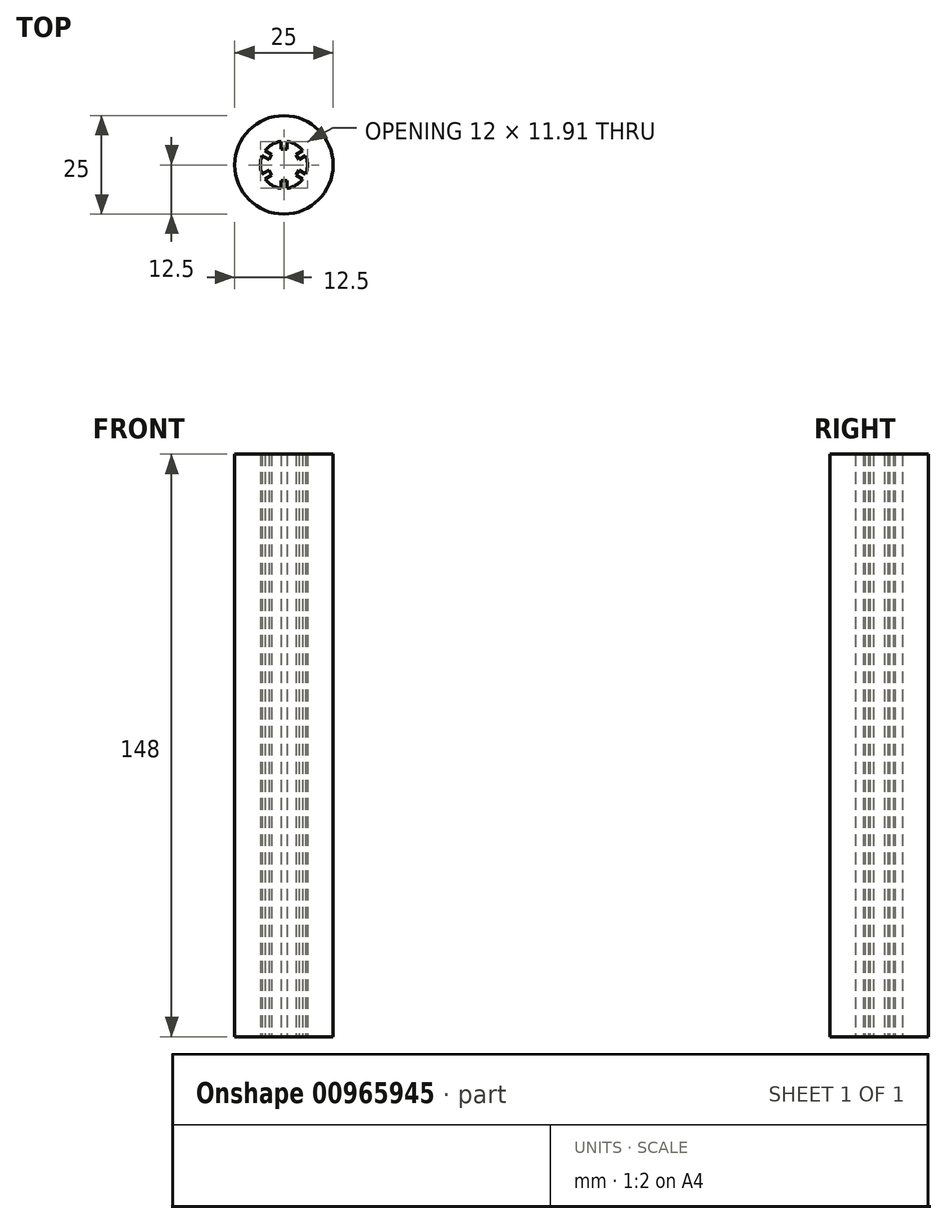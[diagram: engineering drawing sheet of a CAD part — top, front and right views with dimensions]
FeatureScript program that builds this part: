
annotation { "Feature Type Name" : "Feature", "Feature Type Description" : "" }
export const myFeature = defineFeature(function(context is Context, id is Id, definition is map)
    precondition{}
    {
        {
            var Q0;
            Q0=qCreatedBy(makeId("Top.planeOp"),FACE);
            var sketch = newSketch(context, id + "F0", { "sketchPlane" : qUnion([Q0])});
            skCircle(sketch, "E0", {"center": v(0, 0) * mm, "radius": 4 * mm, "construction": true});
            skCircle(sketch, "E1", {"center": v(0, 0) * mm, "radius": 6 * mm});
            skCircle(sketch, "E2", {"center": v(0, 0) * mm, "radius": 12.5 * mm});
            skLineSegment(sketch, "E3.bottom", {"start": v(-0.75, 6) * mm, "end": v(0.75, 6) * mm});
            skLineSegment(sketch, "E3.top", {"start": v(-0.75, 4) * mm, "end": v(0.75, 4) * mm});
            skLineSegment(sketch, "E3.left", {"start": v(-0.75, 6) * mm, "end": v(-0.75, 4) * mm});
            skLineSegment(sketch, "E3.right", {"start": v(0.75, 6) * mm, "end": v(0.75, 4) * mm});
            skLineSegment(sketch, "E4.1.0", {"start": v(-5.57, 2.35) * mm, "end": v(-3.84, 1.35) * mm});
            skLineSegment(sketch, "E4.1.1", {"start": v(-4.82, 3.65) * mm, "end": v(-3.09, 2.65) * mm});
            skLineSegment(sketch, "E4.1.2", {"start": v(-3.84, 1.35) * mm, "end": v(-3.09, 2.65) * mm});
            skLineSegment(sketch, "E4.1.3", {"start": v(-5.57, 2.35) * mm, "end": v(-4.82, 3.65) * mm});
            skLineSegment(sketch, "E4.2.0", {"start": v(-4.82, -3.65) * mm, "end": v(-3.09, -2.65) * mm});
            skLineSegment(sketch, "E4.2.1", {"start": v(-5.57, -2.35) * mm, "end": v(-3.84, -1.35) * mm});
            skLineSegment(sketch, "E4.2.2", {"start": v(-3.09, -2.65) * mm, "end": v(-3.84, -1.35) * mm});
            skLineSegment(sketch, "E4.2.3", {"start": v(-4.82, -3.65) * mm, "end": v(-5.57, -2.35) * mm});
            skLineSegment(sketch, "E5.2.3.0", {"start": v(0.75, -6) * mm, "end": v(0.75, -4) * mm});
            skLineSegment(sketch, "E5.3.3.0", {"start": v(-0.75, -6) * mm, "end": v(-0.75, -4) * mm});
            skLineSegment(sketch, "E5.6.3.0", {"start": v(0.75, -4) * mm, "end": v(-0.75, -4) * mm});
            skLineSegment(sketch, "E5.9.3.0", {"start": v(0.75, -6) * mm, "end": v(-0.75, -6) * mm});
            skLineSegment(sketch, "E5.2.4.0", {"start": v(5.57, -2.35) * mm, "end": v(3.84, -1.35) * mm});
            skLineSegment(sketch, "E5.3.4.0", {"start": v(4.82, -3.65) * mm, "end": v(3.09, -2.65) * mm});
            skLineSegment(sketch, "E5.6.4.0", {"start": v(3.84, -1.35) * mm, "end": v(3.09, -2.65) * mm});
            skLineSegment(sketch, "E5.9.4.0", {"start": v(5.57, -2.35) * mm, "end": v(4.82, -3.65) * mm});
            skLineSegment(sketch, "E5.2.5.0", {"start": v(4.82, 3.65) * mm, "end": v(3.09, 2.65) * mm});
            skLineSegment(sketch, "E5.3.5.0", {"start": v(5.57, 2.35) * mm, "end": v(3.84, 1.35) * mm});
            skLineSegment(sketch, "E5.6.5.0", {"start": v(3.09, 2.65) * mm, "end": v(3.84, 1.35) * mm});
            skLineSegment(sketch, "E5.9.5.0", {"start": v(4.82, 3.65) * mm, "end": v(5.57, 2.35) * mm});
            skPoint(sketch, "E6", {"position": v(0, 4) * mm});
            skSolve(sketch);
        }
        {
            var Q0;
            Q0=makeQuery(id+"F0.imprint","IMPRINT",FACE,{"disambiguationData":[TD([[makeQuery(id+"F0.imprint","IMPRINT",EDGE,{"derivedFrom":sQuery(id+"F0.wireOp",EDGE,"E2")}),1.0]])]});
            var Q1;
            {var subQ0=sQuery(id+"F0.wireOp",EDGE,"E4.1.2");Q1=makeQuery(id+"F0.imprint","IMPRINT",FACE,{"disambiguationData":[TD([[makeQuery(id+"F0.imprint","IMPRINT",EDGE,{"derivedFrom":subQ0}),1.0]])]});}
            var Q2;
            {var subQ0=sQuery(id+"F0.wireOp",EDGE,"E3.top");Q2=makeQuery(id+"F0.imprint","IMPRINT",FACE,{"disambiguationData":[TD([[makeQuery(id+"F0.imprint","IMPRINT",EDGE,{"derivedFrom":subQ0}),1.0]])]});}
            var Q3;
            {var subQ0=sQuery(id+"F0.wireOp",EDGE,"E5.6.5.0");Q3=makeQuery(id+"F0.imprint","IMPRINT",FACE,{"disambiguationData":[TD([[makeQuery(id+"F0.imprint","IMPRINT",EDGE,{"derivedFrom":subQ0}),1.0]])]});}
            var Q4;
            {var subQ0=sQuery(id+"F0.wireOp",EDGE,"E5.6.4.0");Q4=makeQuery(id+"F0.imprint","IMPRINT",FACE,{"disambiguationData":[TD([[makeQuery(id+"F0.imprint","IMPRINT",EDGE,{"derivedFrom":subQ0}),1.0]])]});}
            var Q5;
            {var subQ0=sQuery(id+"F0.wireOp",EDGE,"E5.6.3.0");Q5=makeQuery(id+"F0.imprint","IMPRINT",FACE,{"disambiguationData":[TD([[makeQuery(id+"F0.imprint","IMPRINT",EDGE,{"derivedFrom":subQ0}),1.0]])]});}
            var Q6;
            {var subQ0=sQuery(id+"F0.wireOp",EDGE,"E4.2.2");Q6=makeQuery(id+"F0.imprint","IMPRINT",FACE,{"disambiguationData":[TD([[makeQuery(id+"F0.imprint","IMPRINT",EDGE,{"derivedFrom":subQ0}),1.0]])]});}
            var Q7;
            {var subQ0=sQuery(id+"F0.wireOp",EDGE,"E3.right");var subQ1=sQuery(id+"F0.wireOp",EDGE,"E1");var subQ2=makeQuery(id+"F0.imprint","INTERSECT",VERTEX,{"derivedFrom":[subQ1,subQ0]});Q7=makeQuery(id+"F0.imprint","IMPRINT",FACE,{"disambiguationData":[TD([[makeQuery(id+"F0.imprint","IMPRINT",EDGE,{"disambiguationData":[TD([[subQ2,-1.0]])],"derivedFrom":subQ1}),-1.0]])]});}
            var Q8;
            {var subQ0=sQuery(id+"F0.wireOp",EDGE,"E3.bottom");var subQ1=sQuery(id+"F0.wireOp",EDGE,"E1");var subQ2=makeQuery(id+"F0.imprint","INTERSECT",VERTEX,{"derivedFrom":[subQ1,subQ0]});Q8=makeQuery(id+"F0.imprint","IMPRINT",FACE,{"disambiguationData":[TD([[makeQuery(id+"F0.imprint","IMPRINT",EDGE,{"disambiguationData":[TD([[subQ2,-1.0]])],"derivedFrom":subQ1}),-1.0]])]});}
            var Q9;
            {var subQ0=sQuery(id+"F0.wireOp",EDGE,"E4.1.1");var subQ1=sQuery(id+"F0.wireOp",EDGE,"E1");var subQ2=makeQuery(id+"F0.imprint","INTERSECT",VERTEX,{"derivedFrom":[subQ1,subQ0]});Q9=makeQuery(id+"F0.imprint","IMPRINT",FACE,{"disambiguationData":[TD([[makeQuery(id+"F0.imprint","IMPRINT",EDGE,{"disambiguationData":[TD([[subQ2,-1.0]])],"derivedFrom":subQ1}),-1.0]])]});}
            var Q10;
            {var subQ0=sQuery(id+"F0.wireOp",EDGE,"E5.9.5.0");var subQ1=sQuery(id+"F0.wireOp",EDGE,"E1");var subQ2=makeQuery(id+"F0.imprint","INTERSECT",VERTEX,{"derivedFrom":[subQ1,subQ0]});Q10=makeQuery(id+"F0.imprint","IMPRINT",FACE,{"disambiguationData":[TD([[makeQuery(id+"F0.imprint","IMPRINT",EDGE,{"disambiguationData":[TD([[subQ2,-1.0]])],"derivedFrom":subQ1}),-1.0]])]});}
            var Q11;
            {var subQ0=sQuery(id+"F0.wireOp",EDGE,"E5.9.3.0");var subQ1=sQuery(id+"F0.wireOp",EDGE,"E1");var subQ2=makeQuery(id+"F0.imprint","INTERSECT",VERTEX,{"derivedFrom":[subQ1,subQ0]});Q11=makeQuery(id+"F0.imprint","IMPRINT",FACE,{"disambiguationData":[TD([[makeQuery(id+"F0.imprint","IMPRINT",EDGE,{"disambiguationData":[TD([[subQ2,-1.0]])],"derivedFrom":subQ1}),-1.0]])]});}
            var Q12;
            {var subQ0=sQuery(id+"F0.wireOp",EDGE,"E5.3.4.0");var subQ1=sQuery(id+"F0.wireOp",EDGE,"E1");var subQ2=makeQuery(id+"F0.imprint","INTERSECT",VERTEX,{"derivedFrom":[subQ1,subQ0]});Q12=makeQuery(id+"F0.imprint","IMPRINT",FACE,{"disambiguationData":[TD([[makeQuery(id+"F0.imprint","IMPRINT",EDGE,{"disambiguationData":[TD([[subQ2,-1.0]])],"derivedFrom":subQ1}),-1.0]])]});}
            var Q13;
            {var subQ0=sQuery(id+"F0.wireOp",EDGE,"E5.9.5.0");var subQ1=sQuery(id+"F0.wireOp",EDGE,"E1");var subQ2=makeQuery(id+"F0.imprint","INTERSECT",VERTEX,{"derivedFrom":[subQ1,subQ0]});Q13=makeQuery(id+"F0.imprint","IMPRINT",FACE,{"disambiguationData":[TD([[makeQuery(id+"F0.imprint","IMPRINT",EDGE,{"disambiguationData":[TD([[subQ2,1.0]])],"derivedFrom":subQ1}),-1.0]])]});}
            var Q14;
            {var subQ0=sQuery(id+"F0.wireOp",EDGE,"E4.1.3");var subQ1=sQuery(id+"F0.wireOp",EDGE,"E1");var subQ2=makeQuery(id+"F0.imprint","INTERSECT",VERTEX,{"derivedFrom":[subQ1,subQ0]});Q14=makeQuery(id+"F0.imprint","IMPRINT",FACE,{"disambiguationData":[TD([[makeQuery(id+"F0.imprint","IMPRINT",EDGE,{"disambiguationData":[TD([[subQ2,-1.0]])],"derivedFrom":subQ1}),-1.0]])]});}
            var Q15;
            {var subQ0=sQuery(id+"F0.wireOp",EDGE,"E4.2.1");var subQ1=sQuery(id+"F0.wireOp",EDGE,"E1");var subQ2=makeQuery(id+"F0.imprint","INTERSECT",VERTEX,{"derivedFrom":[subQ1,subQ0]});Q15=makeQuery(id+"F0.imprint","IMPRINT",FACE,{"disambiguationData":[TD([[makeQuery(id+"F0.imprint","IMPRINT",EDGE,{"disambiguationData":[TD([[subQ2,-1.0]])],"derivedFrom":subQ1}),-1.0]])]});}
            var Q16;
            {var subQ0=sQuery(id+"F0.wireOp",EDGE,"E4.2.3");var subQ1=sQuery(id+"F0.wireOp",EDGE,"E1");var subQ2=makeQuery(id+"F0.imprint","INTERSECT",VERTEX,{"derivedFrom":[subQ1,subQ0]});Q16=makeQuery(id+"F0.imprint","IMPRINT",FACE,{"disambiguationData":[TD([[makeQuery(id+"F0.imprint","IMPRINT",EDGE,{"disambiguationData":[TD([[subQ2,-1.0]])],"derivedFrom":subQ1}),-1.0]])]});}
            var Q17;
            {var subQ0=sQuery(id+"F0.wireOp",EDGE,"E5.3.3.0");var subQ1=sQuery(id+"F0.wireOp",EDGE,"E1");var subQ2=makeQuery(id+"F0.imprint","INTERSECT",VERTEX,{"derivedFrom":[subQ1,subQ0]});Q17=makeQuery(id+"F0.imprint","IMPRINT",FACE,{"disambiguationData":[TD([[makeQuery(id+"F0.imprint","IMPRINT",EDGE,{"disambiguationData":[TD([[subQ2,-1.0]])],"derivedFrom":subQ1}),-1.0]])]});}
            var Q18;
            {var subQ0=sQuery(id+"F0.wireOp",EDGE,"E5.9.4.0");var subQ1=sQuery(id+"F0.wireOp",EDGE,"E1");var subQ2=makeQuery(id+"F0.imprint","INTERSECT",VERTEX,{"derivedFrom":[subQ1,subQ0]});Q18=makeQuery(id+"F0.imprint","IMPRINT",FACE,{"disambiguationData":[TD([[makeQuery(id+"F0.imprint","IMPRINT",EDGE,{"disambiguationData":[TD([[subQ2,-1.0]])],"derivedFrom":subQ1}),-1.0]])]});}
            extrude(context, id + "F1", {"entities" : qUnion([Q0, Q1, Q2, Q3, Q4, Q5, Q6, Q7, Q8, Q9, Q10, Q11, Q12, Q13, Q14, Q15, Q16, Q17, Q18]), "depth" : 148 * mm, "offsetDistance" : 25 * mm});
        }
    });
